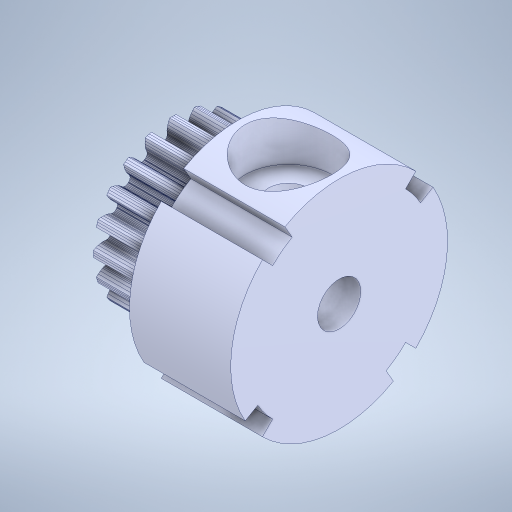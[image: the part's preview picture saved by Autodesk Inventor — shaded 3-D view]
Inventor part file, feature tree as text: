
AUTODESK INVENTOR PART (.ipt)
format: ipt  version: 2023.5 (Build 275446000, 446)  size: 2,191,360 bytes
history: native  units: mm
features: sketch x7, extrude x5, other x4, projected_geometry x3, pattern_circular x1, hole x1, mirror x1
ambient origin geometry x8: Origin, YZ Plane, XZ Plane, XY Plane, X Axis, Y Axis, Z Axis, Center Point
bodies: Body1 (feature_tree)
feature tree (22):
  extrude  "Wyciągnięcie proste1"  Depth=15.0mm
  extrude  "Wyciągnięcie proste2"  Depth=7.0mm TaperAngle=0.0deg
  sketch  "Szkic3"
  other  "Płaszczyzna konstrukcyjna2"
  extrude  "Wyciągnięcie proste3"  Depth=1.0mm TaperAngle=0.0deg
  pattern_circular  "Szyk kołowy1"  [2 undecoded]
  extrude  "Wyciągnięcie proste4"  TaperAngle=15.0deg  [1 undecoded]
  hole  "Otwór1"  [1 undecoded]
  mirror  "Odbij1"
  extrude  "Wyciągnięcie proste5"  TaperAngle=0.0deg  [1 undecoded]
  other  "Bryła31"
  sketch  "Szkic1"
  sketch  "Szkic2"
  projected_geometry  "Pętla rzutowana1"
  other  "Płaszczyzna konstrukcyjna1"
  sketch  "Szkic5"
  sketch  "Szkic6"
  projected_geometry  "Pętla rzutowana2"
  sketch  "Szkic7"
  sketch  "Szkic8"
  projected_geometry  "Pętla rzutowana3"
  other  "Engrane_8:1"
note: 5 required parameter values undecoded (feature->parameter linkage not recoverable at this tier; creation-order binding heuristic only, values carry confidence <= 0.55)
